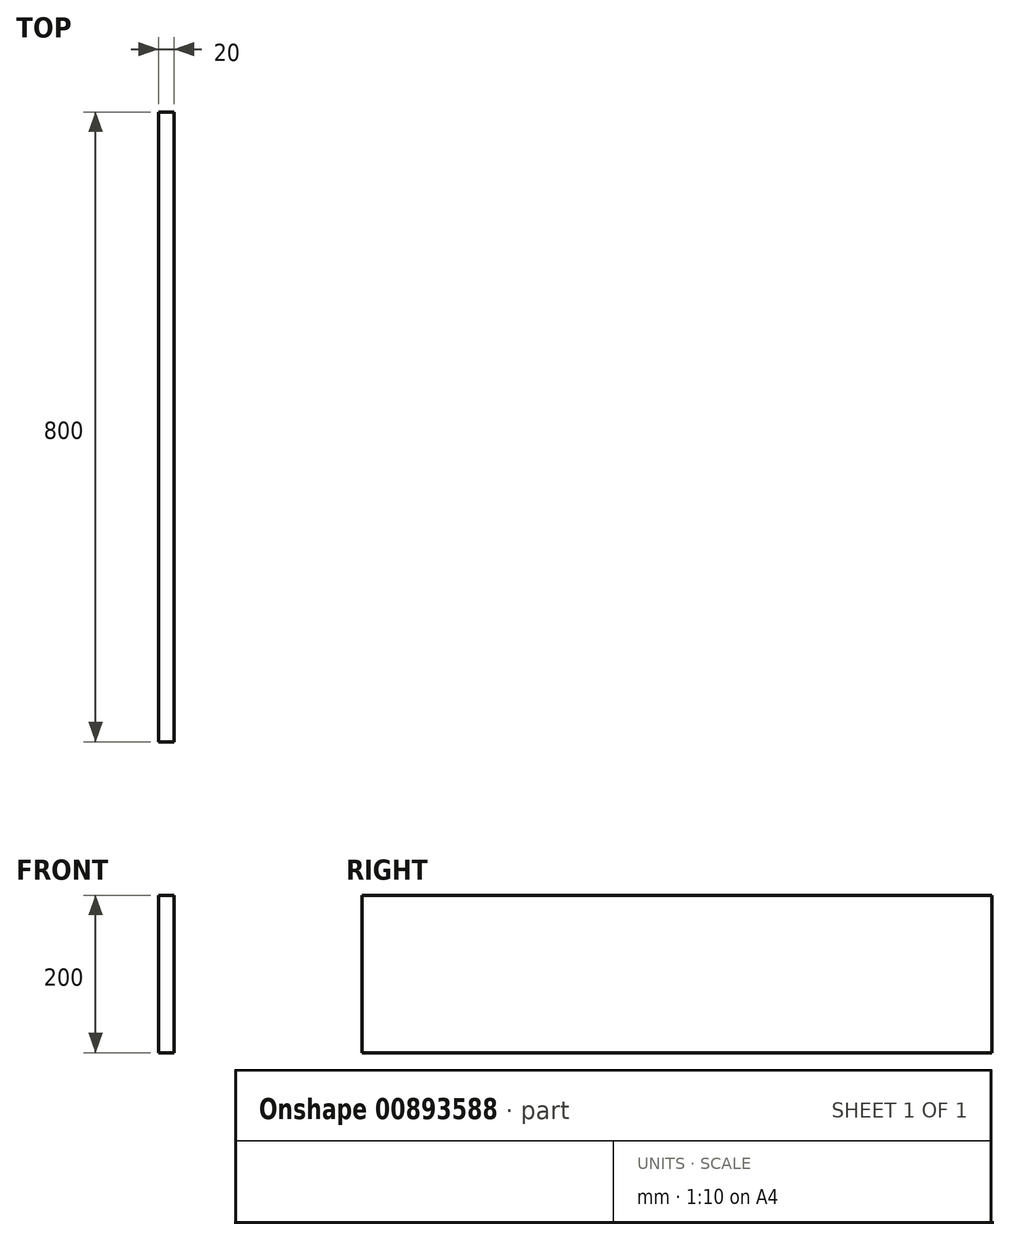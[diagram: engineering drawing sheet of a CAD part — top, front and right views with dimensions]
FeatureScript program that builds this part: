
annotation { "Feature Type Name" : "Feature", "Feature Type Description" : "" }
export const myFeature = defineFeature(function(context is Context, id is Id, definition is map)
    precondition{}
    {
        {
            var Q0;
            Q0=qCreatedBy(makeId("Front.planeOp"),FACE);
            var sketch = newSketch(context, id + "F0", { "sketchPlane" : qUnion([Q0])});
            skLineSegment(sketch, "E0.bottom", {"start": v(0, 20) * mm, "end": v(20, 20) * mm});
            skLineSegment(sketch, "E0.top", {"start": v(0, -180) * mm, "end": v(20, -180) * mm});
            skLineSegment(sketch, "E0.left", {"start": v(0, 20) * mm, "end": v(0, -180) * mm});
            skLineSegment(sketch, "E0.right", {"start": v(20, 20) * mm, "end": v(20, -180) * mm});
            skSolve(sketch);
        }
        {
            var Q0;
            Q0=qSketchRegion(id+"F0",true);
            extrude(context, id + "F1", {"entities" : qUnion([Q0]), "oppositeDirection" : true, "depth" : 800 * mm, "offsetDistance" : 25 * mm});
        }
    });
